# Revit family: WashbasinUnit-Vitra-EqualSeries-64079
name_source: partatom
category: Furniture Systems
revit_build: Autodesk Revit 2017 (Build: 20160225_1515(x64)
units: mm (PartAtom-declared; Revit-internal decimal feet)

## family parameters
Cut with Voids When Loaded = No
Host = Face
OmniClass Number = 23.40.00.00
OmniClass Title = Equipment and Furnishings
Part Type = Normal
Room Calculation Point = No
Round Connector Dimension = Use Diameter
Shared = Yes

## types (3) — shared parameters
BIMobject category = Bathroom compound units
Construction Type = Face Mounted
Default Elevation = 580 mm  [stored 1.90289 ft]
Depth = 440 mm  [stored 1.44357 ft]
Design country = Turkey
Height = 88 mm
IFC Classification = Furniture
Manufacturer = Vitra
Manufacturer name = Vitra
Masterformat 2014 Code = 13 42 13
Masterformat 2014 Description = Bathroom Unit Modules
NBS Referans Code = 35-75-08
NBS Referans Description = Bathroom Cabinets
Nominal height = 0.000
Nominal width = 0.000
OmniClass Code = 23-31 25 13
OmniClass Description = Bathroom Cabinets
Primary Material = Vitra-Crome
Product certification = https://vitraglobal.com
Product data url = https://www.vitraglobal.com
Product family = Equal
Product group = Washbasin Unit
Secondary Material = Vitra-Crome
Thrid Material = Vitra-AmericanValnut
UNSPSC Code = 301815
UNSPSC Description = Bathroom Cabinets
URL = https://vitraglobal.com
Uniclass 1.4 Code = L8241
Uniclass 1.4 Description = Bathroom Cabinets
Uniclass 2.0 Code = PR-35-75-08
Uniclass 2.0 Description = Bathroom Cabinets
Uniclass 2015 Code = Pr_40_20_93
Uniclass 2015 Name = Wash basins, sinks and troughs
Uniformat II Code = E20
Uniformat II Description = FURNISHINGS
Warranty Period (Year) = 2
Youtube = https://www.youtube.com

## per-type parameters (varying)
| type | Article No. (default) | Description | Model | Product SKU | Technical description | Weight Net (kg) | Width |
| WashbasinUnit-40cm-Vitra-EqualSeries_64079 | 64079 | Equal Washbasin Unit, 40 cm, with Towel Holder | 64079 | 64079 | https://www.vitra.com.tr | 31,200 | 468 mm |
| WashbasinUnit-80cm-Vitra-EqualSeries_64083 | 64083 | Equal Washbasin Unit, 80 cm, with Towel Holder | 64083 | 64083 | https://www.vitraglobal.com | 32 | 838 mm |
| WashbasinUnit-60cm-Vitra-EqualSeries_64081 | 64081 | Equal Washbasin Unit, 60 cm, with Towel Holder | 64081 | 64081 | https://www.vitraglobal.com | 24 | 638 mm  [stored 2.09318 ft] |

note: [stored X ft] marks values corroborated as IEEE doubles in the binary element streams (Revit-internal decimal feet)

## geometry (parser evidence)
native form markers: Sweep x2
no freeform markers — native parametric forms only
